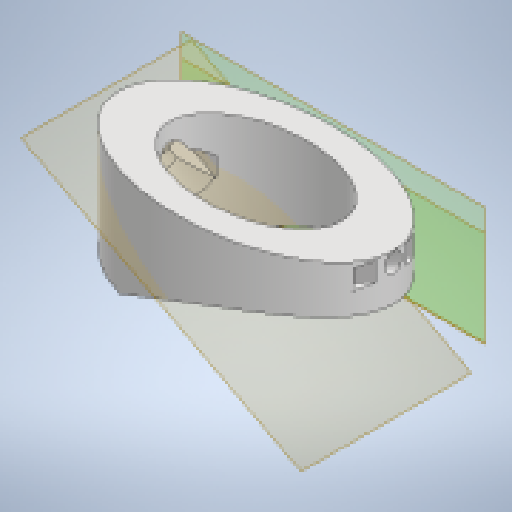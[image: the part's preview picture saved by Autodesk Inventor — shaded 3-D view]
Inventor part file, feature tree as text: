
AUTODESK INVENTOR PART (.ipt)
format: ipt  version: 2025.1 (Build 291241000, 241)  size: 545,792 bytes
history: native  units: mm
features: plane x7, sketch x7, extrude x6, chamfer x3, projected_geometry x2, mirror x1, fillet x1
ambient origin geometry x8: Origin, YZ Plane, XZ Plane, XY Plane, X Axis, Y Axis, Z Axis, Center Point
bodies: Volumenkörper1 (feature_tree)
feature tree (27):
  extrude  "Extrusion1"  Depth=20.0mm
  plane  "Arbeitsebene1"
  plane  "Arbeitsebene3"
  extrude  "Extrusion4"  Depth=12.0mm
  extrude  "Extrusion5"  Depth=4.886922mm
  extrude  "Extrusion6"  Depth=14.0mm
  sketch  "Skizze8"  dims[d14=4.0mm]
  plane  "Arbeitsebene4"
  chamfer  "Fasen1"  Distance=10.0mm
  plane  "Arbeitsebene6"
  mirror  "Spiegeln2"
  extrude  "Extrusion8"  Depth=4.0mm
  plane  "Arbeitsebene8"
  extrude  "Extrusion9"  Depth=10.0mm TaperAngle=0.0deg
  chamfer  "Fasen2"  Distance=3.0mm
  chamfer  "Fasen3"  [1 undecoded]
  fillet  "Rundung1"  Radius=6.108652mm
  sketch  "Skizze1"  dims[d0=32.0mm d1=20.0mm]
  plane  "Arbeitsebene2"
  sketch  "Skizze5"  dims[d2=25.0mm d3=0.0mm d4=12.0mm]
  sketch  "Skizze6"  dims[d5=18.0mm d10=4.886922mm d11=-18.5mm]
  projected_geometry  "Projizierte Kontur2"
  sketch  "Skizze7"  dims[d12=8.0mm d13=14.0mm]
  projected_geometry  "Projizierte Kontur3"
  sketch  "Skizze10"  dims[d15=5.0mm d16=10.0mm d17=0.0mm]
  plane  "Arbeitsebene7"
  sketch  "Skizze11"  dims[d18=0.0mm d19=0.0mm d20=4.0mm d21=10.0mm d22=0.0mm d23=3.0mm d24=2.0mm d25=6.632251mm d28=0.0mm d29=0.0mm d30=6.108652mm d31=-20.0mm d32=10.0mm d33=0.0mm d36=5.0mm d37=2.0mm d38=45.0deg d39=3.0mm d40=2.0mm d41=45.0deg d42=3.0mm]
note: 1 required parameter value undecoded (feature->parameter linkage not recoverable at this tier; creation-order binding heuristic only, values carry confidence <= 0.55)
